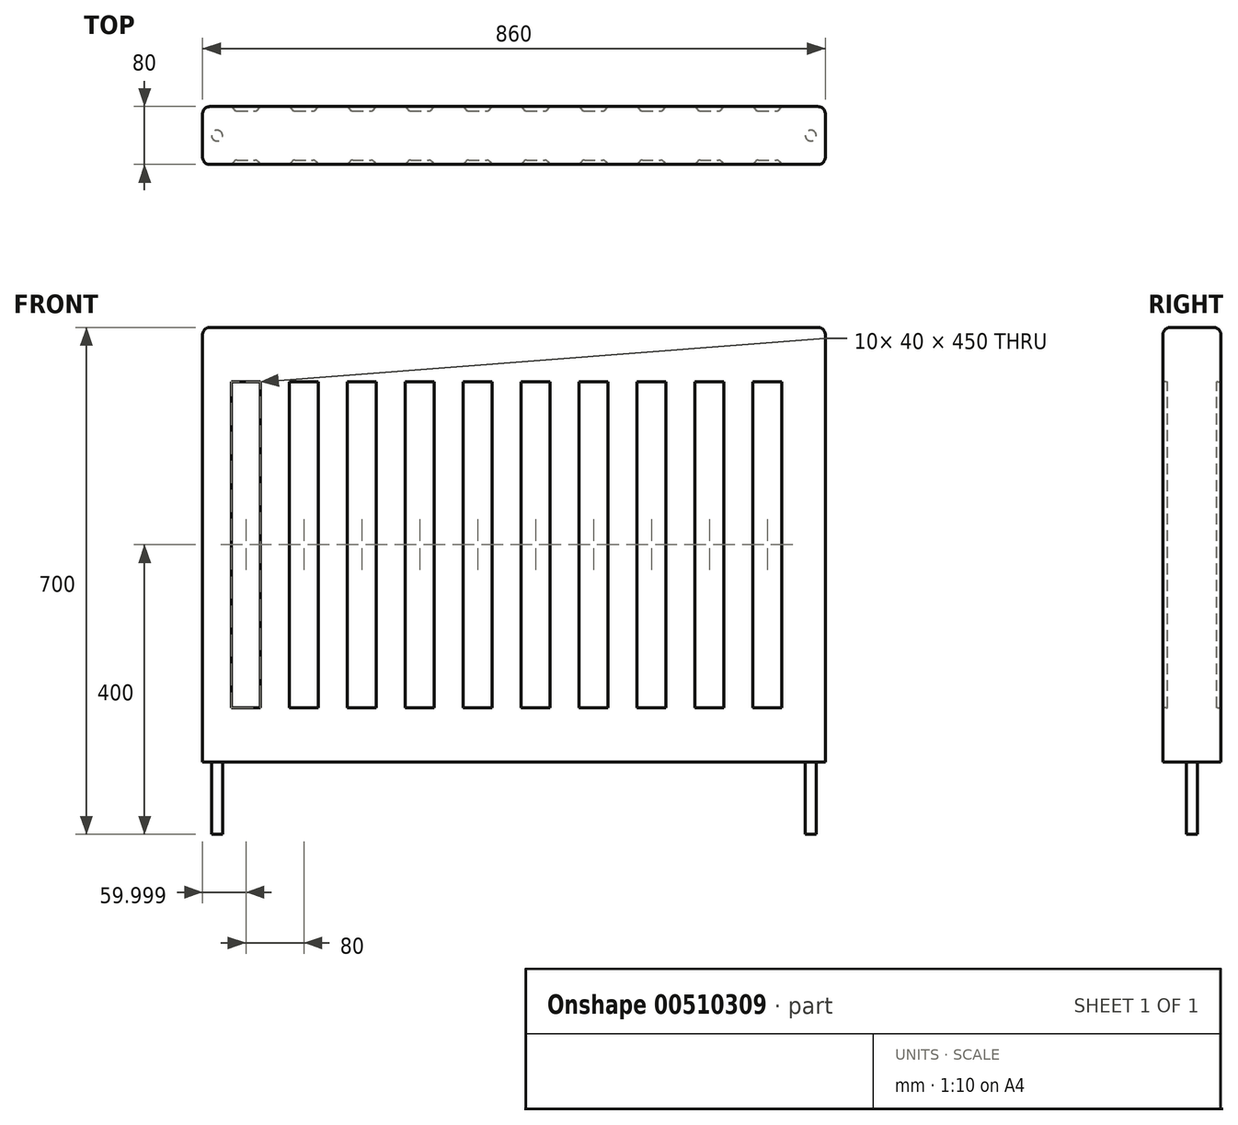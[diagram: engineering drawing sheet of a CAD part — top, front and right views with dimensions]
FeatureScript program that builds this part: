
annotation { "Feature Type Name" : "Feature", "Feature Type Description" : "" }
export const myFeature = defineFeature(function(context is Context, id is Id, definition is map)
    precondition{}
    {
        {
            var Q0;
            Q0=qCreatedBy(makeId("Top.planeOp"),FACE);
            var sketch = newSketch(context, id + "F0", { "sketchPlane" : qUnion([Q0])});
            skLineSegment(sketch, "E0.bottom", {"start": v(-345.66, -18.68) * mm, "end": v(514.34, -18.68) * mm});
            skLineSegment(sketch, "E0.top", {"start": v(-345.66, -98.68) * mm, "end": v(514.34, -98.68) * mm});
            skLineSegment(sketch, "E0.left", {"start": v(-345.66, -18.68) * mm, "end": v(-345.66, -98.68) * mm});
            skLineSegment(sketch, "E0.right", {"start": v(514.34, -18.68) * mm, "end": v(514.34, -98.68) * mm});
            skSolve(sketch);
        }
        {
            var Q0;
            Q0=makeQuery(id+"F0.imprint","IMPRINT",FACE,{"disambiguationData":[TD([[makeQuery(id+"F0.imprint","IMPRINT",EDGE,{"derivedFrom":sQuery(id+"F0.wireOp",EDGE,"E0.bottom")}),-1.0]])]});
            extrude(context, id + "F1", {"entities" : qUnion([Q0]), "endBound" : BoundingType.SYMMETRIC, "depth" : 600 * mm});
        }
        {
            var Q0;
            Q0=makeQuery(id+"F1.opExtrude","CAP_FACE",FACE,{"disambiguationData":[OSD([sQuery(id+"F0.wireOp",EDGE,"E0.bottom"),sQuery(id+"F0.wireOp",EDGE,"E0.top"),sQuery(id+"F0.wireOp",EDGE,"E0.left"),sQuery(id+"F0.wireOp",EDGE,"E0.right")])],"isStart":true});
            var sketch = newSketch(context, id + "F2", { "sketchPlane" : qUnion([Q0])});
            skCircle(sketch, "E1", {"center": v(-325.66, 58.68) * mm, "radius": 7.5 * mm});
            skPoint(sketch, "E1.centerSnap0", {"position": v(-345.66, 58.68) * mm});
            skCircle(sketch, "E2", {"center": v(494.34, 58.68) * mm, "radius": 7.5 * mm});
            skPoint(sketch, "E2.centerSnap0", {"position": v(514.34, 58.68) * mm});
            skSolve(sketch);
        }
        {
            var Q0;
            Q0=makeQuery(id+"F2.imprint","IMPRINT",FACE,{"disambiguationData":[TD([[makeQuery(id+"F2.imprint","IMPRINT",EDGE,{"derivedFrom":sQuery(id+"F2.wireOp",EDGE,"E2")}),1.0]])]});
            var Q1;
            Q1=makeQuery(id+"F2.imprint","IMPRINT",FACE,{"disambiguationData":[TD([[makeQuery(id+"F2.imprint","IMPRINT",EDGE,{"derivedFrom":sQuery(id+"F2.wireOp",EDGE,"E1")}),1.0]])]});
            extrude(context, id + "F3", {"entities" : qUnion([Q0, Q1]), "operationType" : NewBodyOperationType.ADD, "depth" : 100 * mm});
        }
        {
            var Q0;
            Q0=qCreatedBy(makeId("Top.planeOp"),FACE);
            var sketch = newSketch(context, id + "F4", { "sketchPlane" : qUnion([Q0])});
            skLineSegment(sketch, "E3", {"start": v(-305.66, -18.68) * mm, "end": v(-302.12, -22.9) * mm});
            skLineSegment(sketch, "E4", {"start": v(-298.3, -24.68) * mm, "end": v(-273.03, -24.68) * mm});
            skLineSegment(sketch, "E5", {"start": v(-269.2, -22.9) * mm, "end": v(-265.66, -18.68) * mm});
            skPoint(sketch, "E6.visualSharp", {"position": v(-300.63, -24.68) * mm});
            skArc(sketch, "E6.filletArc", {"start": v(-302.12, -22.9) * mm, "mid": v(-300.4, -24.22) * mm, "end": v(-298.3, -24.68) * mm});
            skPoint(sketch, "E7.visualSharp", {"position": v(-270.7, -24.68) * mm});
            skArc(sketch, "E7.filletArc", {"start": v(-273.03, -24.68) * mm, "mid": v(-270.91, -24.22) * mm, "end": v(-269.2, -22.9) * mm});
            skLineSegment(sketch, "E8.1.0.0", {"start": v(-225.66, -18.68) * mm, "end": v(-222.12, -22.9) * mm});
            skArc(sketch, "E8.1.0.1", {"start": v(-222.12, -22.9) * mm, "mid": v(-220.4, -24.22) * mm, "end": v(-218.3, -24.68) * mm});
            skLineSegment(sketch, "E8.1.0.2", {"start": v(-218.3, -24.68) * mm, "end": v(-193.03, -24.68) * mm});
            skArc(sketch, "E8.1.0.3", {"start": v(-193.03, -24.68) * mm, "mid": v(-190.91, -24.22) * mm, "end": v(-189.2, -22.9) * mm});
            skLineSegment(sketch, "E8.1.0.4", {"start": v(-189.2, -22.9) * mm, "end": v(-185.66, -18.68) * mm});
            skLineSegment(sketch, "E8.2.0.0", {"start": v(-145.66, -18.68) * mm, "end": v(-142.12, -22.9) * mm});
            skArc(sketch, "E8.2.0.1", {"start": v(-142.12, -22.9) * mm, "mid": v(-140.4, -24.22) * mm, "end": v(-138.3, -24.68) * mm});
            skLineSegment(sketch, "E8.2.0.2", {"start": v(-138.3, -24.68) * mm, "end": v(-113.03, -24.68) * mm});
            skArc(sketch, "E8.2.0.3", {"start": v(-113.03, -24.68) * mm, "mid": v(-110.91, -24.22) * mm, "end": v(-109.2, -22.9) * mm});
            skLineSegment(sketch, "E8.2.0.4", {"start": v(-109.2, -22.9) * mm, "end": v(-105.66, -18.68) * mm});
            skLineSegment(sketch, "E8.3.0.0", {"start": v(-65.66, -18.68) * mm, "end": v(-62.12, -22.9) * mm});
            skArc(sketch, "E8.3.0.1", {"start": v(-62.12, -22.9) * mm, "mid": v(-60.4, -24.22) * mm, "end": v(-58.3, -24.68) * mm});
            skLineSegment(sketch, "E8.3.0.2", {"start": v(-58.3, -24.68) * mm, "end": v(-33.03, -24.68) * mm});
            skArc(sketch, "E8.3.0.3", {"start": v(-33.03, -24.68) * mm, "mid": v(-30.91, -24.22) * mm, "end": v(-29.2, -22.9) * mm});
            skLineSegment(sketch, "E8.3.0.4", {"start": v(-29.2, -22.9) * mm, "end": v(-25.66, -18.68) * mm});
            skLineSegment(sketch, "E8.4.0.0", {"start": v(14.34, -18.68) * mm, "end": v(17.88, -22.9) * mm});
            skArc(sketch, "E8.4.0.1", {"start": v(17.88, -22.9) * mm, "mid": v(19.6, -24.22) * mm, "end": v(21.7, -24.68) * mm});
            skLineSegment(sketch, "E8.4.0.2", {"start": v(21.7, -24.68) * mm, "end": v(46.97, -24.68) * mm});
            skArc(sketch, "E8.4.0.3", {"start": v(46.97, -24.68) * mm, "mid": v(49.09, -24.22) * mm, "end": v(50.8, -22.9) * mm});
            skLineSegment(sketch, "E8.4.0.4", {"start": v(50.8, -22.9) * mm, "end": v(54.34, -18.68) * mm});
            skLineSegment(sketch, "E8.5.0.0", {"start": v(94.34, -18.68) * mm, "end": v(97.88, -22.9) * mm});
            skArc(sketch, "E8.5.0.1", {"start": v(97.88, -22.9) * mm, "mid": v(99.6, -24.22) * mm, "end": v(101.7, -24.68) * mm});
            skLineSegment(sketch, "E8.5.0.2", {"start": v(101.7, -24.68) * mm, "end": v(126.97, -24.68) * mm});
            skArc(sketch, "E8.5.0.3", {"start": v(126.97, -24.68) * mm, "mid": v(129.09, -24.22) * mm, "end": v(130.8, -22.9) * mm});
            skLineSegment(sketch, "E8.5.0.4", {"start": v(130.8, -22.9) * mm, "end": v(134.34, -18.68) * mm});
            skLineSegment(sketch, "E8.6.0.0", {"start": v(174.34, -18.68) * mm, "end": v(177.88, -22.9) * mm});
            skArc(sketch, "E8.6.0.1", {"start": v(177.88, -22.9) * mm, "mid": v(179.6, -24.22) * mm, "end": v(181.7, -24.68) * mm});
            skLineSegment(sketch, "E8.6.0.2", {"start": v(181.7, -24.68) * mm, "end": v(206.97, -24.68) * mm});
            skArc(sketch, "E8.6.0.3", {"start": v(206.97, -24.68) * mm, "mid": v(209.09, -24.22) * mm, "end": v(210.8, -22.9) * mm});
            skLineSegment(sketch, "E8.6.0.4", {"start": v(210.8, -22.9) * mm, "end": v(214.34, -18.68) * mm});
            skLineSegment(sketch, "E8.7.0.0", {"start": v(254.34, -18.68) * mm, "end": v(257.88, -22.9) * mm});
            skArc(sketch, "E8.7.0.1", {"start": v(257.88, -22.9) * mm, "mid": v(259.6, -24.22) * mm, "end": v(261.7, -24.68) * mm});
            skLineSegment(sketch, "E8.7.0.2", {"start": v(261.7, -24.68) * mm, "end": v(286.97, -24.68) * mm});
            skArc(sketch, "E8.7.0.3", {"start": v(286.97, -24.68) * mm, "mid": v(289.09, -24.22) * mm, "end": v(290.8, -22.9) * mm});
            skLineSegment(sketch, "E8.7.0.4", {"start": v(290.8, -22.9) * mm, "end": v(294.34, -18.68) * mm});
            skLineSegment(sketch, "E8.8.0.0", {"start": v(334.34, -18.68) * mm, "end": v(337.88, -22.9) * mm});
            skArc(sketch, "E8.8.0.1", {"start": v(337.88, -22.9) * mm, "mid": v(339.6, -24.22) * mm, "end": v(341.7, -24.68) * mm});
            skLineSegment(sketch, "E8.8.0.2", {"start": v(341.7, -24.68) * mm, "end": v(366.97, -24.68) * mm});
            skArc(sketch, "E8.8.0.3", {"start": v(366.97, -24.68) * mm, "mid": v(369.09, -24.22) * mm, "end": v(370.8, -22.9) * mm});
            skLineSegment(sketch, "E8.8.0.4", {"start": v(370.8, -22.9) * mm, "end": v(374.34, -18.68) * mm});
            skLineSegment(sketch, "E8.9.0.0", {"start": v(414.34, -18.68) * mm, "end": v(417.88, -22.9) * mm});
            skArc(sketch, "E8.9.0.1", {"start": v(417.88, -22.9) * mm, "mid": v(419.6, -24.22) * mm, "end": v(421.7, -24.68) * mm});
            skLineSegment(sketch, "E8.9.0.2", {"start": v(421.7, -24.68) * mm, "end": v(446.97, -24.68) * mm});
            skArc(sketch, "E8.9.0.3", {"start": v(446.97, -24.68) * mm, "mid": v(449.09, -24.22) * mm, "end": v(450.8, -22.9) * mm});
            skLineSegment(sketch, "E8.9.0.4", {"start": v(450.8, -22.9) * mm, "end": v(454.34, -18.68) * mm});
            skLineSegment(sketch, "E9", {"start": v(-345.66, -58.68) * mm, "end": v(514.34, -58.68) * mm, "construction": true});
            skArc(sketch, "E10.MirrorCS", {"start": v(-302.12, -94.47) * mm, "mid": v(-300.4, -93.15) * mm, "end": v(-298.3, -92.68) * mm});
            skLineSegment(sketch, "E11.MirrorCS", {"start": v(-305.66, -98.68) * mm, "end": v(-302.12, -94.47) * mm});
            skLineSegment(sketch, "E12.MirrorCS", {"start": v(-269.2, -94.47) * mm, "end": v(-265.66, -98.68) * mm});
            skLineSegment(sketch, "E13.MirrorCS", {"start": v(-225.66, -98.68) * mm, "end": v(-222.12, -94.47) * mm});
            skArc(sketch, "E14.MirrorCS", {"start": v(-273.03, -92.68) * mm, "mid": v(-270.91, -93.15) * mm, "end": v(-269.2, -94.47) * mm});
            skArc(sketch, "E15.MirrorCS", {"start": v(-222.12, -94.47) * mm, "mid": v(-220.4, -93.15) * mm, "end": v(-218.3, -92.68) * mm});
            skArc(sketch, "E16.MirrorCS", {"start": v(286.97, -92.68) * mm, "mid": v(289.09, -93.15) * mm, "end": v(290.8, -94.47) * mm});
            skLineSegment(sketch, "E17.MirrorCS", {"start": v(-65.66, -98.68) * mm, "end": v(-62.12, -94.47) * mm});
            skLineSegment(sketch, "E18.MirrorCS", {"start": v(-109.2, -94.47) * mm, "end": v(-105.66, -98.68) * mm});
            skArc(sketch, "E19.MirrorCS", {"start": v(-113.03, -92.68) * mm, "mid": v(-110.91, -93.15) * mm, "end": v(-109.2, -94.47) * mm});
            skLineSegment(sketch, "E20.MirrorCS", {"start": v(414.34, -98.68) * mm, "end": v(417.88, -94.47) * mm});
            skLineSegment(sketch, "E21.MirrorCS", {"start": v(14.34, -98.68) * mm, "end": v(17.88, -94.47) * mm});
            skArc(sketch, "E22.MirrorCS", {"start": v(257.88, -94.47) * mm, "mid": v(259.6, -93.15) * mm, "end": v(261.7, -92.68) * mm});
            skLineSegment(sketch, "E23.MirrorCS", {"start": v(130.8, -94.47) * mm, "end": v(134.34, -98.68) * mm});
            skArc(sketch, "E24.MirrorCS", {"start": v(366.97, -92.68) * mm, "mid": v(369.09, -93.15) * mm, "end": v(370.8, -94.47) * mm});
            skArc(sketch, "E25.MirrorCS", {"start": v(417.88, -94.47) * mm, "mid": v(419.6, -93.15) * mm, "end": v(421.7, -92.68) * mm});
            skArc(sketch, "E26.MirrorCS", {"start": v(17.88, -94.47) * mm, "mid": v(19.6, -93.15) * mm, "end": v(21.7, -92.68) * mm});
            skLineSegment(sketch, "E27.MirrorCS", {"start": v(174.34, -98.68) * mm, "end": v(177.88, -94.47) * mm});
            skLineSegment(sketch, "E28.MirrorCS", {"start": v(-29.2, -94.47) * mm, "end": v(-25.66, -98.68) * mm});
            skLineSegment(sketch, "E29.MirrorCS", {"start": v(254.34, -98.68) * mm, "end": v(257.88, -94.47) * mm});
            skArc(sketch, "E30.MirrorCS", {"start": v(97.88, -94.47) * mm, "mid": v(99.6, -93.15) * mm, "end": v(101.7, -92.68) * mm});
            skArc(sketch, "E31.MirrorCS", {"start": v(-33.03, -92.68) * mm, "mid": v(-30.91, -93.15) * mm, "end": v(-29.2, -94.47) * mm});
            skLineSegment(sketch, "E32.MirrorCS", {"start": v(210.8, -94.47) * mm, "end": v(214.34, -98.68) * mm});
            skLineSegment(sketch, "E33.MirrorCS", {"start": v(94.34, -98.68) * mm, "end": v(97.88, -94.47) * mm});
            skArc(sketch, "E34.MirrorCS", {"start": v(337.88, -94.47) * mm, "mid": v(339.6, -93.15) * mm, "end": v(341.7, -92.68) * mm});
            skArc(sketch, "E35.MirrorCS", {"start": v(-142.12, -94.47) * mm, "mid": v(-140.4, -93.15) * mm, "end": v(-138.3, -92.68) * mm});
            skArc(sketch, "E36.MirrorCS", {"start": v(126.97, -92.68) * mm, "mid": v(129.09, -93.15) * mm, "end": v(130.8, -94.47) * mm});
            skLineSegment(sketch, "E37.MirrorCS", {"start": v(370.8, -94.47) * mm, "end": v(374.34, -98.68) * mm});
            skArc(sketch, "E38.MirrorCS", {"start": v(206.97, -92.68) * mm, "mid": v(209.09, -93.15) * mm, "end": v(210.8, -94.47) * mm});
            skLineSegment(sketch, "E39.MirrorCS", {"start": v(50.8, -94.47) * mm, "end": v(54.34, -98.68) * mm});
            skLineSegment(sketch, "E40.MirrorCS", {"start": v(334.34, -98.68) * mm, "end": v(337.88, -94.47) * mm});
            skLineSegment(sketch, "E41.MirrorCS", {"start": v(450.8, -94.47) * mm, "end": v(454.34, -98.68) * mm});
            skLineSegment(sketch, "E42.MirrorCS", {"start": v(-145.66, -98.68) * mm, "end": v(-142.12, -94.47) * mm});
            skLineSegment(sketch, "E43.MirrorCS", {"start": v(-189.2, -94.47) * mm, "end": v(-185.66, -98.68) * mm});
            skArc(sketch, "E44.MirrorCS", {"start": v(-193.03, -92.68) * mm, "mid": v(-190.91, -93.15) * mm, "end": v(-189.2, -94.47) * mm});
            skArc(sketch, "E45.MirrorCS", {"start": v(46.97, -92.68) * mm, "mid": v(49.09, -93.15) * mm, "end": v(50.8, -94.47) * mm});
            skLineSegment(sketch, "E46.MirrorCS", {"start": v(290.8, -94.47) * mm, "end": v(294.34, -98.68) * mm});
            skArc(sketch, "E47.MirrorCS", {"start": v(177.88, -94.47) * mm, "mid": v(179.6, -93.15) * mm, "end": v(181.7, -92.68) * mm});
            skArc(sketch, "E48.MirrorCS", {"start": v(-62.12, -94.47) * mm, "mid": v(-60.4, -93.15) * mm, "end": v(-58.3, -92.68) * mm});
            skArc(sketch, "E49.MirrorCS", {"start": v(446.97, -92.68) * mm, "mid": v(449.09, -93.15) * mm, "end": v(450.8, -94.47) * mm});
            skLineSegment(sketch, "E50.MirrorCS", {"start": v(-298.3, -92.68) * mm, "end": v(-273.03, -92.68) * mm});
            skLineSegment(sketch, "E51.MirrorCS", {"start": v(21.7, -92.68) * mm, "end": v(46.97, -92.68) * mm});
            skLineSegment(sketch, "E52.MirrorCS", {"start": v(421.7, -92.68) * mm, "end": v(446.97, -92.68) * mm});
            skLineSegment(sketch, "E53.MirrorCS", {"start": v(181.7, -92.68) * mm, "end": v(206.97, -92.68) * mm});
            skLineSegment(sketch, "E54.MirrorCS", {"start": v(101.7, -92.68) * mm, "end": v(126.97, -92.68) * mm});
            skLineSegment(sketch, "E55.MirrorCS", {"start": v(261.7, -92.68) * mm, "end": v(286.97, -92.68) * mm});
            skPoint(sketch, "E56.MirrorP", {"position": v(-270.7, -92.68) * mm});
            skLineSegment(sketch, "E57.MirrorCS", {"start": v(341.7, -92.68) * mm, "end": v(366.97, -92.68) * mm});
            skLineSegment(sketch, "E58.MirrorCS", {"start": v(-138.3, -92.68) * mm, "end": v(-113.03, -92.68) * mm});
            skLineSegment(sketch, "E59.MirrorCS", {"start": v(-58.3, -92.68) * mm, "end": v(-33.03, -92.68) * mm});
            skPoint(sketch, "E60.MirrorP", {"position": v(-300.63, -92.68) * mm});
            skLineSegment(sketch, "E61.MirrorCS", {"start": v(-218.3, -92.68) * mm, "end": v(-193.03, -92.68) * mm});
            skLineSegment(sketch, "E62", {"start": v(-305.66, -18.68) * mm, "end": v(-265.66, -18.68) * mm});
            skLineSegment(sketch, "E63", {"start": v(-225.66, -18.68) * mm, "end": v(-185.66, -18.68) * mm});
            skLineSegment(sketch, "E64", {"start": v(-145.66, -18.68) * mm, "end": v(-105.66, -18.68) * mm});
            skLineSegment(sketch, "E65", {"start": v(-65.66, -18.68) * mm, "end": v(-25.66, -18.68) * mm});
            skLineSegment(sketch, "E66", {"start": v(14.34, -18.68) * mm, "end": v(54.34, -18.68) * mm});
            skLineSegment(sketch, "E67", {"start": v(94.34, -18.68) * mm, "end": v(134.34, -18.68) * mm});
            skLineSegment(sketch, "E68", {"start": v(174.34, -18.68) * mm, "end": v(214.34, -18.68) * mm});
            skLineSegment(sketch, "E69", {"start": v(254.34, -18.68) * mm, "end": v(294.34, -18.68) * mm});
            skLineSegment(sketch, "E70", {"start": v(334.34, -18.68) * mm, "end": v(374.34, -18.68) * mm});
            skLineSegment(sketch, "E71", {"start": v(414.34, -18.68) * mm, "end": v(454.34, -18.68) * mm});
            skLineSegment(sketch, "E72", {"start": v(454.34, -98.68) * mm, "end": v(414.34, -98.68) * mm});
            skLineSegment(sketch, "E73", {"start": v(374.34, -98.68) * mm, "end": v(334.34, -98.68) * mm});
            skLineSegment(sketch, "E74", {"start": v(294.34, -98.68) * mm, "end": v(254.34, -98.68) * mm});
            skLineSegment(sketch, "E75", {"start": v(214.34, -98.68) * mm, "end": v(174.34, -98.68) * mm});
            skLineSegment(sketch, "E76", {"start": v(134.34, -98.68) * mm, "end": v(94.34, -98.68) * mm});
            skLineSegment(sketch, "E77", {"start": v(54.34, -98.68) * mm, "end": v(14.34, -98.68) * mm});
            skLineSegment(sketch, "E78", {"start": v(-25.66, -98.68) * mm, "end": v(-65.66, -98.68) * mm});
            skLineSegment(sketch, "E79", {"start": v(-105.66, -98.68) * mm, "end": v(-145.66, -98.68) * mm});
            skLineSegment(sketch, "E80", {"start": v(-185.66, -98.68) * mm, "end": v(-225.66, -98.68) * mm});
            skLineSegment(sketch, "E81", {"start": v(-265.66, -98.68) * mm, "end": v(-305.66, -98.68) * mm});
            skSolve(sketch);
        }
        {
            var Q0;
            Q0=qSketchRegion(id+"F4",true);
            extrude(context, id + "F5", {"entities" : qUnion([Q0]), "operationType" : NewBodyOperationType.REMOVE, "endBound" : BoundingType.SYMMETRIC, "oppositeDirection" : true, "depth" : 450 * mm});
        }
        {
            var Q0;
            Q0=makeQuery(id+"F1.opExtrude","SWEPT_EDGE",EDGE,{"disambiguationData":[OSD([sQuery(id+"F0.wireOp",EDGE,"E0.top"),sQuery(id+"F0.wireOp",EDGE,"E0.left")])]});
            var Q1;
            Q1=makeQuery(id+"F1.opExtrude","SWEPT_EDGE",EDGE,{"disambiguationData":[OSD([sQuery(id+"F0.wireOp",EDGE,"E0.bottom"),sQuery(id+"F0.wireOp",EDGE,"E0.left")])]});
            var Q2;
            Q2=makeQuery(id+"F1.opExtrude","SWEPT_EDGE",EDGE,{"disambiguationData":[OSD([sQuery(id+"F0.wireOp",EDGE,"E0.top"),sQuery(id+"F0.wireOp",EDGE,"E0.right")])]});
            var Q3;
            Q3=makeQuery(id+"F1.opExtrude","SWEPT_EDGE",EDGE,{"disambiguationData":[OSD([sQuery(id+"F0.wireOp",EDGE,"E0.bottom"),sQuery(id+"F0.wireOp",EDGE,"E0.right")])]});
            var Q4;
            Q4=makeQuery(id+"F1.opExtrude","CAP_EDGE",EDGE,{"disambiguationData":[OSD([sQuery(id+"F0.wireOp",EDGE,"E0.top")])],"isStart":false});
            var Q5;
            Q5=makeQuery(id+"F1.opExtrude","CAP_EDGE",EDGE,{"disambiguationData":[OSD([sQuery(id+"F0.wireOp",EDGE,"E0.bottom")])],"isStart":false});
            var Q6;
            Q6=makeQuery(id+"F1.opExtrude","CAP_EDGE",EDGE,{"disambiguationData":[OSD([sQuery(id+"F0.wireOp",EDGE,"E0.right")])],"isStart":false});
            var Q7;
            Q7=makeQuery(id+"F1.opExtrude","CAP_EDGE",EDGE,{"disambiguationData":[OSD([sQuery(id+"F0.wireOp",EDGE,"E0.left")])],"isStart":false});
            fillet(context, id + "F6", {"entities" : qUnion([Q0, Q1, Q2, Q3, Q4, Q5, Q6, Q7]), "radius" : 10 * mm, "tangentPropagation" : true, "allowEdgeOverflow" : false});
        }
    });
